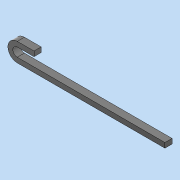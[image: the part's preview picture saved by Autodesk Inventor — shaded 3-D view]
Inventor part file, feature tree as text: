
AUTODESK INVENTOR PART (.ipt)
format: ipt  version: 2020 (Build 240168000, 168)  size: 87,040 bytes
history: native  units: mm
features: extrude x1, sketch x1
ambient origin geometry x8: Origin, YZ Plane, XZ Plane, XY Plane, X Axis, Y Axis, Z Axis, Center Point
bodies: Solid1 (feature_tree)
feature tree (2):
  extrude  "Extrusion1"  Depth=20.0mm
  sketch  "Sketch1"  dims[d0=76.0mm d1=20.0mm d2=20.0mm d4=600.0mm d5=29.0mm d6=0.0mm d7=68.0mm]
